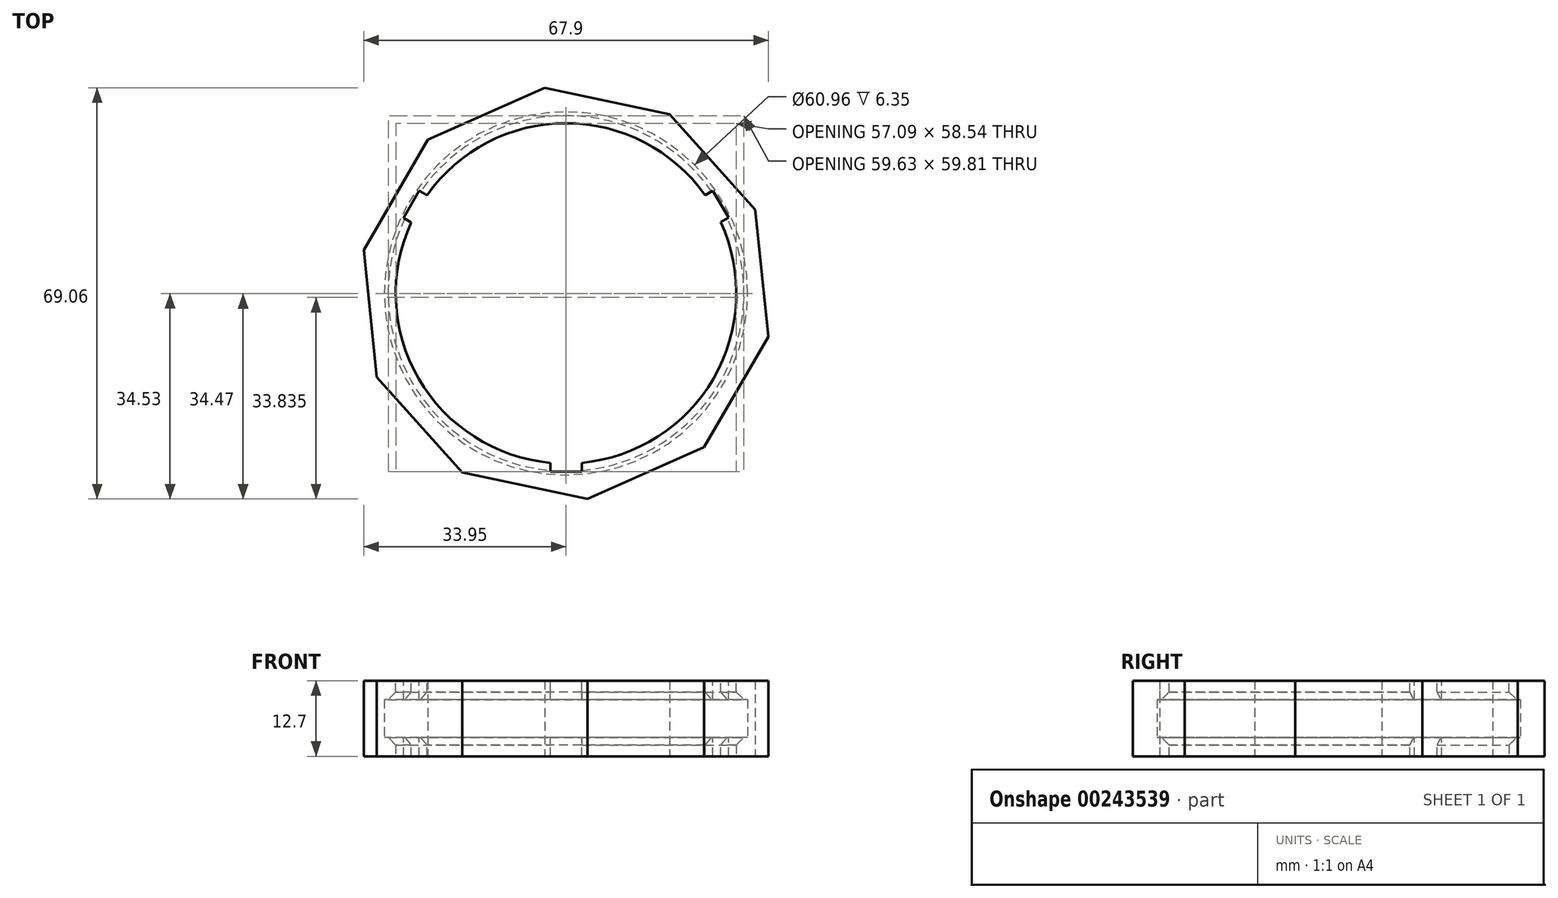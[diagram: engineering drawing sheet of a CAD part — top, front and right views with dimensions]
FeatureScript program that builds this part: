
annotation { "Feature Type Name" : "Feature", "Feature Type Description" : "" }
export const myFeature = defineFeature(function(context is Context, id is Id, definition is map)
    precondition{}
    {
        {
            var Q0;
            Q0=qCreatedBy(makeId("Top.planeOp"),FACE);
            var sketch = newSketch(context, id + "F0", { "sketchPlane" : qUnion([Q0])});
            skCircle(sketch, "E0.cCircle", {"center": v(0, 0) * mm, "radius": 33.02 * mm, "construction": true});
            skLineSegment(sketch, "E0.0", {"start": v(33.95, -7.27) * mm, "end": v(23.2, -25.84) * mm});
            skLineSegment(sketch, "E0.1", {"start": v(23.2, -25.84) * mm, "end": v(3.58, -34.53) * mm});
            skLineSegment(sketch, "E0.2", {"start": v(3.58, -34.53) * mm, "end": v(-17.4, -30.04) * mm});
            skLineSegment(sketch, "E0.3", {"start": v(-17.4, -30.04) * mm, "end": v(-31.74, -14.07) * mm});
            skLineSegment(sketch, "E0.4", {"start": v(-31.74, -14.07) * mm, "end": v(-33.95, 7.27) * mm});
            skLineSegment(sketch, "E0.5", {"start": v(-33.95, 7.27) * mm, "end": v(-23.2, 25.84) * mm});
            skLineSegment(sketch, "E0.6", {"start": v(-23.2, 25.84) * mm, "end": v(-3.58, 34.53) * mm});
            skLineSegment(sketch, "E0.7", {"start": v(-3.58, 34.53) * mm, "end": v(17.4, 30.04) * mm});
            skLineSegment(sketch, "E0.8", {"start": v(17.4, 30.04) * mm, "end": v(31.74, 14.07) * mm});
            skLineSegment(sketch, "E0.9", {"start": v(31.74, 14.07) * mm, "end": v(33.95, -7.27) * mm});
            skPoint(sketch, "E0.0.midPoint", {"position": v(28.57, -16.55) * mm});
            skCircle(sketch, "E1", {"center": v(0, 0) * mm, "radius": 30.48 * mm});
            skCircle(sketch, "E2", {"center": v(0, 0) * mm, "radius": 28.58 * mm});
            skSolve(sketch);
        }
        {
            var Q0;
            Q0=makeQuery(id+"F0.imprint","IMPRINT",FACE,{"disambiguationData":[TD([[makeQuery(id+"F0.imprint","IMPRINT",EDGE,{"derivedFrom":sQuery(id+"F0.wireOp",EDGE,"E0.0")}),-1.0]])]});
            extrude(context, id + "F1", {"entities" : qUnion([Q0]), "depth" : 12.7 * mm});
        }
        {
            var Q0;
            Q0=qCreatedBy(makeId("Top.planeOp"),FACE);
            var sketch = newSketch(context, id + "F2", { "sketchPlane" : qUnion([Q0])});
            skCircle(sketch, "E3", {"center": v(0, 0) * mm, "radius": 30.48 * mm});
            skCircle(sketch, "E4", {"center": v(0, 0) * mm, "radius": 28.58 * mm});
            skSolve(sketch);
        }
        {
            var Q0;
            Q0=makeQuery(id+"F2.imprint","IMPRINT",FACE,{"disambiguationData":[TD([[makeQuery(id+"F2.imprint","IMPRINT",EDGE,{"derivedFrom":sQuery(id+"F2.wireOp",EDGE,"E3")}),1.0]])]});
            extrude(context, id + "F3", {"entities" : qUnion([Q0]), "operationType" : NewBodyOperationType.ADD, "depth" : 3.17 * mm});
        }
        {
            var Q0;
            Q0=makeQuery(id+"F1.opExtrude","CAP_FACE",FACE,{"disambiguationData":[OSD([sQuery(id+"F0.wireOp",EDGE,"E0.0"),sQuery(id+"F0.wireOp",EDGE,"E0.1"),sQuery(id+"F0.wireOp",EDGE,"E0.2"),sQuery(id+"F0.wireOp",EDGE,"E0.3"),sQuery(id+"F0.wireOp",EDGE,"E0.4"),sQuery(id+"F0.wireOp",EDGE,"E0.5"),sQuery(id+"F0.wireOp",EDGE,"E0.6"),sQuery(id+"F0.wireOp",EDGE,"E0.7"),sQuery(id+"F0.wireOp",EDGE,"E0.8"),sQuery(id+"F0.wireOp",EDGE,"E0.9"),sQuery(id+"F0.wireOp",EDGE,"E1")])],"isStart":false});
            var sketch = newSketch(context, id + "F4", { "sketchPlane" : qUnion([Q0])});
            skCircle(sketch, "E5", {"center": v(0, 0) * mm, "radius": 30.48 * mm});
            skCircle(sketch, "E6", {"center": v(0, 0) * mm, "radius": 28.58 * mm});
            skSolve(sketch);
        }
        {
            var Q0;
            Q0=makeQuery(id+"F4.imprint","IMPRINT",FACE,{"disambiguationData":[TD([[makeQuery(id+"F4.imprint","IMPRINT",EDGE,{"derivedFrom":sQuery(id+"F4.wireOp",EDGE,"E5")}),1.0]])]});
            extrude(context, id + "F5", {"entities" : qUnion([Q0]), "operationType" : NewBodyOperationType.ADD, "oppositeDirection" : true, "depth" : 3.17 * mm});
        }
        {
            var Q0;
            Q0=makeQuery(id+"F5.boolean.opBoolean","MERGE",FACE,{"derivedFrom":[makeQuery(id+"F1.opExtrude","CAP_FACE",FACE,{"disambiguationData":[OSD([sQuery(id+"F0.wireOp",EDGE,"E0.0"),sQuery(id+"F0.wireOp",EDGE,"E0.1"),sQuery(id+"F0.wireOp",EDGE,"E0.2"),sQuery(id+"F0.wireOp",EDGE,"E0.3"),sQuery(id+"F0.wireOp",EDGE,"E0.4"),sQuery(id+"F0.wireOp",EDGE,"E0.5"),sQuery(id+"F0.wireOp",EDGE,"E0.6"),sQuery(id+"F0.wireOp",EDGE,"E0.7"),sQuery(id+"F0.wireOp",EDGE,"E0.8"),sQuery(id+"F0.wireOp",EDGE,"E0.9"),sQuery(id+"F0.wireOp",EDGE,"E1")])],"isStart":false}),makeQuery(id+"F5.opExtrude","CAP_FACE",FACE,{"disambiguationData":[OSD([sQuery(id+"F4.wireOp",EDGE,"E5"),sQuery(id+"F4.wireOp",EDGE,"E6")])],"isStart":true})]});
            var sketch = newSketch(context, id + "F6", { "sketchPlane" : qUnion([Q0])});
            skCircle(sketch, "E7.cCircle", {"center": v(0, 0) * mm, "radius": 3.04 * mm, "construction": true});
            skLineSegment(sketch, "E7.0", {"start": v(2.63, -1.52) * mm, "end": v(-2.63, -1.52) * mm});
            skLineSegment(sketch, "E7.1", {"start": v(-2.63, -1.52) * mm, "end": v(0, 3.04) * mm});
            skLineSegment(sketch, "E7.2", {"start": v(0, 3.04) * mm, "end": v(2.63, -1.52) * mm});
            skLineSegment(sketch, "E8.bottom", {"start": v(-2.63, -1.52) * mm, "end": v(2.63, -1.52) * mm});
            skLineSegment(sketch, "E8.top", {"start": v(-2.63, -29.97) * mm, "end": v(2.63, -29.97) * mm});
            skLineSegment(sketch, "E8.left", {"start": v(-2.63, -1.52) * mm, "end": v(-2.63, -29.97) * mm});
            skLineSegment(sketch, "E8.right", {"start": v(2.63, -1.52) * mm, "end": v(2.63, -29.97) * mm});
            skLineSegment(sketch, "E9.bottom", {"start": v(-24.64, 17.26) * mm, "end": v(0, 3.04) * mm});
            skLineSegment(sketch, "E9.top", {"start": v(-27.27, 12.7) * mm, "end": v(-2.64, -1.53) * mm});
            skLineSegment(sketch, "E9.left", {"start": v(-24.64, 17.26) * mm, "end": v(-27.27, 12.7) * mm});
            skLineSegment(sketch, "E9.right", {"start": v(0, 3.04) * mm, "end": v(-2.64, -1.53) * mm});
            skLineSegment(sketch, "E10.bottom", {"start": v(0, 3.04) * mm, "end": v(24.64, 17.26) * mm});
            skLineSegment(sketch, "E10.top", {"start": v(2.63, -1.52) * mm, "end": v(27.27, 12.7) * mm});
            skLineSegment(sketch, "E10.right", {"start": v(24.64, 17.26) * mm, "end": v(27.27, 12.7) * mm});
            skSolve(sketch);
        }
        {
            var Q0;
            {var subQ0=sQuery(id+"F6.wireOp",EDGE,"E9.left");Q0=makeQuery(id+"F6.imprint","IMPRINT",FACE,{"disambiguationData":[TD([[makeQuery(id+"F6.imprint","IMPRINT",EDGE,{"derivedFrom":subQ0}),1.0]])]});}
            var Q1;
            {var subQ0=sQuery(id+"F6.wireOp",EDGE,"E10.right");Q1=makeQuery(id+"F6.imprint","IMPRINT",FACE,{"disambiguationData":[TD([[makeQuery(id+"F6.imprint","IMPRINT",EDGE,{"derivedFrom":subQ0}),-1.0]])]});}
            var Q2;
            {var subQ0=sQuery(id+"F6.wireOp",EDGE,"E8.top");Q2=makeQuery(id+"F6.imprint","IMPRINT",FACE,{"disambiguationData":[TD([[makeQuery(id+"F6.imprint","IMPRINT",EDGE,{"derivedFrom":subQ0}),1.0]])]});}
            extrude(context, id + "F7", {"entities" : qUnion([Q0, Q1, Q2]), "operationType" : NewBodyOperationType.REMOVE, "oppositeDirection" : true, "depth" : 25.4 * mm});
        }
        {
            var Q0;
            {var subQ0=sQuery(id+"F2.wireOp",EDGE,"E4");Q0=makeQuery(id+"F7.boolean.opBoolean","SPLIT",EDGE,{"disambiguationData":[TD([makeQuery(id+"F7.opExtrude","SWEPT_FACE",FACE,{"disambiguationData":[OSD([sQuery(id+"F6.wireOp",EDGE,"E8.left")])]})])],"derivedFrom":makeQuery(id+"F3.opExtrude","CAP_EDGE",EDGE,{"disambiguationData":[OSD([subQ0])],"isStart":false})});}
            var Q1;
            {var subQ0=sQuery(id+"F2.wireOp",EDGE,"E4");Q1=makeQuery(id+"F7.boolean.opBoolean","SPLIT",EDGE,{"disambiguationData":[TD([makeQuery(id+"F7.opExtrude","SWEPT_FACE",FACE,{"disambiguationData":[OSD([sQuery(id+"F6.wireOp",EDGE,"E8.right")])]})])],"derivedFrom":makeQuery(id+"F3.opExtrude","CAP_EDGE",EDGE,{"disambiguationData":[OSD([subQ0])],"isStart":false})});}
            var Q2;
            {var subQ0=sQuery(id+"F4.wireOp",EDGE,"E6");Q2=makeQuery(id+"F7.boolean.opBoolean","SPLIT",EDGE,{"disambiguationData":[TD([makeQuery(id+"F7.opExtrude","SWEPT_FACE",FACE,{"disambiguationData":[OSD([sQuery(id+"F6.wireOp",EDGE,"E8.left")])]})])],"derivedFrom":makeQuery(id+"F5.opExtrude","CAP_EDGE",EDGE,{"disambiguationData":[OSD([subQ0])],"isStart":false})});}
            var Q3;
            {var subQ0=sQuery(id+"F4.wireOp",EDGE,"E6");Q3=makeQuery(id+"F7.boolean.opBoolean","SPLIT",EDGE,{"disambiguationData":[TD([makeQuery(id+"F7.opExtrude","SWEPT_FACE",FACE,{"disambiguationData":[OSD([sQuery(id+"F6.wireOp",EDGE,"E8.right")])]})])],"derivedFrom":makeQuery(id+"F5.opExtrude","CAP_EDGE",EDGE,{"disambiguationData":[OSD([subQ0])],"isStart":false})});}
            var Q4;
            {var subQ0=sQuery(id+"F2.wireOp",EDGE,"E4");Q4=makeQuery(id+"F7.boolean.opBoolean","SPLIT",EDGE,{"disambiguationData":[TD([makeQuery(id+"F7.opExtrude","SWEPT_FACE",FACE,{"disambiguationData":[OSD([sQuery(id+"F6.wireOp",EDGE,"E9.bottom")])]})])],"derivedFrom":makeQuery(id+"F3.opExtrude","CAP_EDGE",EDGE,{"disambiguationData":[OSD([subQ0])],"isStart":false})});}
            var Q5;
            {var subQ0=sQuery(id+"F4.wireOp",EDGE,"E6");Q5=makeQuery(id+"F7.boolean.opBoolean","SPLIT",EDGE,{"disambiguationData":[TD([makeQuery(id+"F7.opExtrude","SWEPT_FACE",FACE,{"disambiguationData":[OSD([sQuery(id+"F6.wireOp",EDGE,"E9.bottom")])]})])],"derivedFrom":makeQuery(id+"F5.opExtrude","CAP_EDGE",EDGE,{"disambiguationData":[OSD([subQ0])],"isStart":false})});}
            chamfer(context, id + "F8", {"entities" : qUnion([Q0, Q1, Q2, Q3, Q4, Q5]), "width" : 1.27 * mm, "tangentPropagation" : true});
        }
    });
